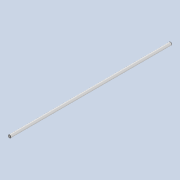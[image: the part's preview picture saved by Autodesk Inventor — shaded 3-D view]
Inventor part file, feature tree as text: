
AUTODESK INVENTOR PART (.ipt)
format: ipt  version: 2020 (Build 240168000, 168)  size: 77,824 bytes
history: native  units: mm
features: extrude x1, chamfer x1, sketch x1
ambient origin geometry x8: Origin, YZ Plane, XZ Plane, XY Plane, X Axis, Y Axis, Z Axis, Center Point
bodies: Solid1 (feature_tree)
feature tree (3):
  extrude  "Extrusion1"  Depth=568.0mm TaperAngle=0.0deg
  chamfer  "Chamfer1"  Distance=0.5mm Angle=45.0deg
  sketch  "Sketch1"  dims[d0=10.0mm d1=568.0mm d2=0.0mm d3=0.5mm d4=2.0mm d5=45.0deg]
